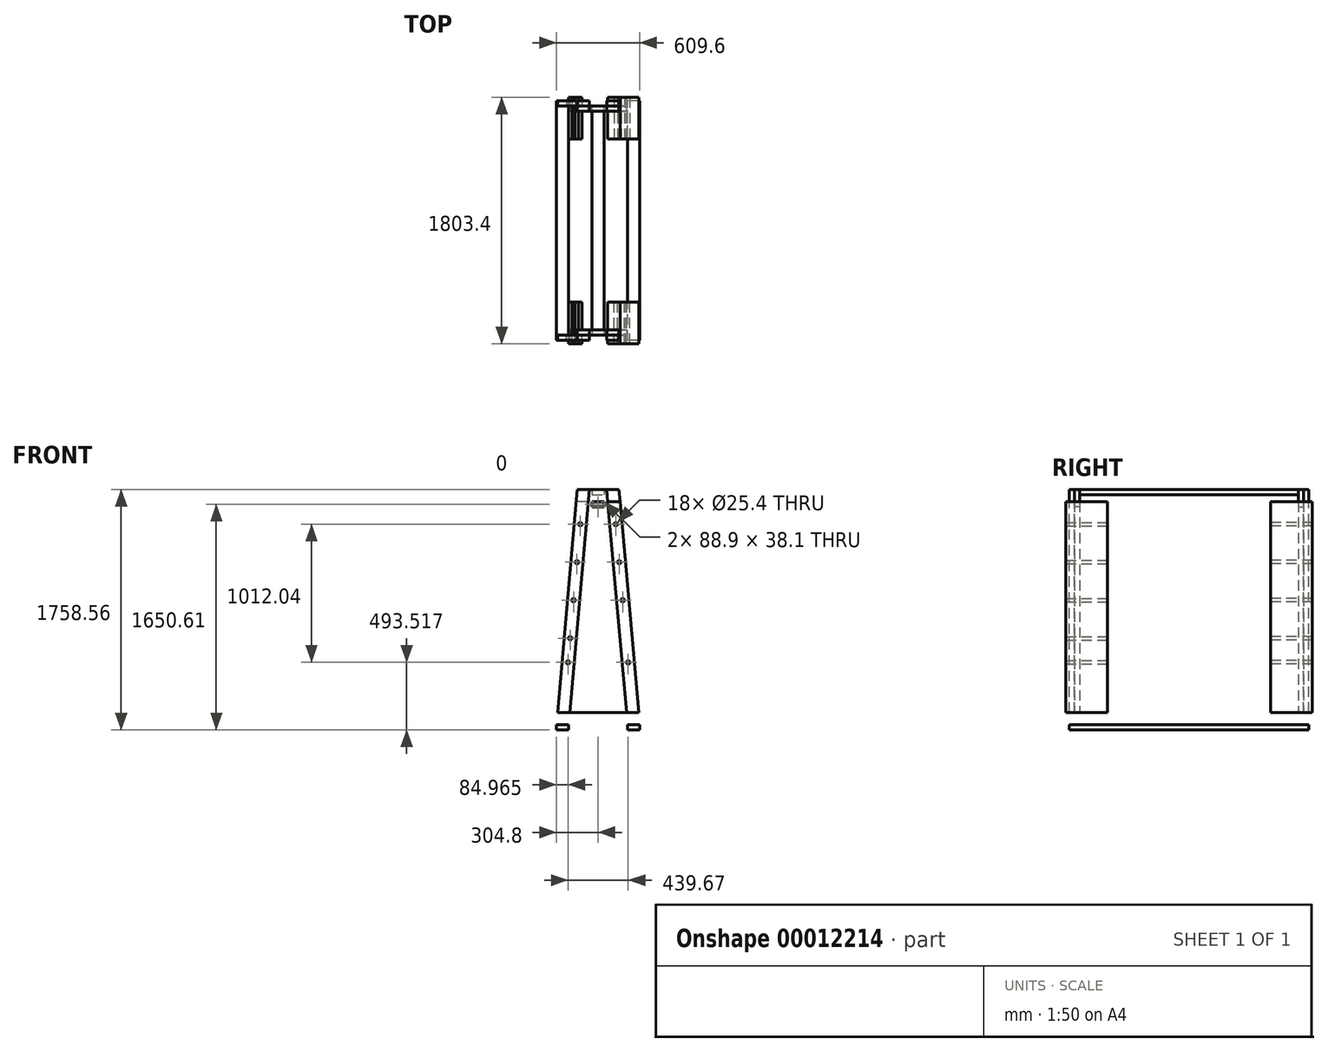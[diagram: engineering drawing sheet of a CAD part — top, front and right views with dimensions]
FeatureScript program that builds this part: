
annotation { "Feature Type Name" : "Feature", "Feature Type Description" : "" }
export const myFeature = defineFeature(function(context is Context, id is Id, definition is map)
    precondition{}
    {
        {
            var Q0;
            Q0=qCreatedBy(makeId("Front.planeOp"),FACE);
            var sketch = newSketch(context, id + "F0", { "sketchPlane" : qUnion([Q0])});
            skLineSegment(sketch, "E0", {"start": v(-304.8, 0) * mm, "end": v(-152.4, 1720.46) * mm});
            skLineSegment(sketch, "E1", {"start": v(-152.4, 1720.46) * mm, "end": v(-63.15, 1720.46) * mm});
            skLineSegment(sketch, "E2", {"start": v(-63.15, 1720.46) * mm, "end": v(-215.55, 0) * mm});
            skLineSegment(sketch, "E3", {"start": v(-215.55, 0) * mm, "end": v(-304.8, 0) * mm});
            skLineSegment(sketch, "E4", {"start": v(215.55, 0) * mm, "end": v(63.15, 1720.46) * mm});
            skLineSegment(sketch, "E5", {"start": v(63.15, 1720.46) * mm, "end": v(152.4, 1720.46) * mm});
            skLineSegment(sketch, "E6", {"start": v(152.4, 1720.46) * mm, "end": v(304.8, 0) * mm});
            skLineSegment(sketch, "E7", {"start": v(304.8, 0) * mm, "end": v(215.55, 0) * mm});
            skLineSegment(sketch, "E8", {"start": v(-107.78, 1720.46) * mm, "end": v(-260.18, 0) * mm, "construction": true});
            skCircle(sketch, "E9", {"center": v(-219.83, 455.42) * mm, "radius": 12.7 * mm});
            skCircle(sketch, "E10", {"center": v(-179.5, 910.83) * mm, "radius": 12.7 * mm});
            skCircle(sketch, "E11", {"center": v(-154.84, 1189.14) * mm, "radius": 12.7 * mm});
            skCircle(sketch, "E12", {"center": v(-130.19, 1467.45) * mm, "radius": 12.7 * mm});
            skLineSegment(sketch, "E13", {"start": v(-63.15, 1720.46) * mm, "end": v(63.15, 1720.46) * mm});
            skLineSegment(sketch, "E14", {"start": v(160.27, 1631.56) * mm, "end": v(-160.27, 1631.56) * mm});
            skLineSegment(sketch, "E15", {"start": v(-215.55, 0) * mm, "end": v(215.55, 0) * mm});
            skLineSegment(sketch, "E16", {"start": v(-296.93, 88.9) * mm, "end": v(296.93, 88.9) * mm});
            skLineSegment(sketch, "E17.bottom", {"start": v(-304.8, 0) * mm, "end": v(304.8, 0) * mm});
            skLineSegment(sketch, "E17.left", {"start": v(-304.8, 0) * mm, "end": v(-304.8, -38.1) * mm});
            skLineSegment(sketch, "E17.right", {"start": v(304.8, 0) * mm, "end": v(304.8, -38.1) * mm});
            skLineSegment(sketch, "E18.bottom", {"start": v(-304.8, -38.1) * mm, "end": v(-215.9, -38.1) * mm});
            skLineSegment(sketch, "E19.bottom", {"start": v(304.8, -38.1) * mm, "end": v(215.9, -38.1) * mm});
            skCircle(sketch, "E20.0.MirrorC", {"center": v(130.19, 1467.45) * mm, "radius": 12.7 * mm});
            skCircle(sketch, "E21.0.MirrorC", {"center": v(154.84, 1189.14) * mm, "radius": 12.7 * mm});
            skCircle(sketch, "E22.0.MirrorC", {"center": v(179.5, 910.83) * mm, "radius": 12.7 * mm});
            skCircle(sketch, "E23.0.MirrorC", {"center": v(219.83, 455.42) * mm, "radius": 12.7 * mm});
            skLineSegment(sketch, "E24.bottom", {"start": v(-44.45, 1720.46) * mm, "end": v(44.45, 1720.46) * mm});
            skLineSegment(sketch, "E24.top", {"start": v(-44.45, 1758.56) * mm, "end": v(44.45, 1758.56) * mm});
            skLineSegment(sketch, "E24.left", {"start": v(-44.45, 1720.46) * mm, "end": v(-44.45, 1758.56) * mm});
            skLineSegment(sketch, "E24.right", {"start": v(44.45, 1720.46) * mm, "end": v(44.45, 1758.56) * mm});
            skLineSegment(sketch, "E25.bottom", {"start": v(44.45, 1631.56) * mm, "end": v(-44.45, 1631.56) * mm});
            skLineSegment(sketch, "E25.top", {"start": v(44.45, 1593.46) * mm, "end": v(-44.45, 1593.46) * mm});
            skLineSegment(sketch, "E25.left", {"start": v(44.45, 1631.56) * mm, "end": v(44.45, 1593.46) * mm});
            skLineSegment(sketch, "E25.right", {"start": v(-44.45, 1631.56) * mm, "end": v(-44.45, 1593.46) * mm});
            skLineSegment(sketch, "E26", {"start": v(215.9, -38.1) * mm, "end": v(215.55, 0) * mm});
            skLineSegment(sketch, "E27", {"start": v(-215.9, -38.1) * mm, "end": v(-215.55, 0) * mm});
            skCircle(sketch, "E28", {"center": v(-204.15, 632.52) * mm, "radius": 12.7 * mm});
            skSolve(sketch);
        }
        {
            var Q0;
            {var subQ5=sQuery(id+"F0.wireOp",EDGE,"E1");Q0=makeQuery(id+"F0.imprint","IMPRINT",FACE,{"disambiguationData":[TD([[makeQuery(id+"F0.imprint","IMPRINT",EDGE,{"derivedFrom":subQ5}),-1.0]])]});}
            var Q1;
            {var subQ5=sQuery(id+"F0.wireOp",EDGE,"E5");Q1=makeQuery(id+"F0.imprint","IMPRINT",FACE,{"disambiguationData":[TD([[makeQuery(id+"F0.imprint","IMPRINT",EDGE,{"derivedFrom":subQ5}),-1.0]])]});}
            var Q2;
            {var subQ0=sQuery(id+"F0.wireOp",EDGE,"E17.bottom");var subQ1=sQuery(id+"F0.wireOp",EDGE,"E2");var subQ2=makeQuery(id+"F0.imprint","INTERSECT",VERTEX,{"derivedFrom":[subQ1,subQ0]});Q2=makeQuery(id+"F0.imprint","IMPRINT",FACE,{"disambiguationData":[TD([[makeQuery(id+"F0.imprint","IMPRINT",EDGE,{"disambiguationData":[TD([[subQ2,1.0]])],"derivedFrom":subQ1}),-1.0]])]});}
            var Q3;
            {var subQ0=sQuery(id+"F0.wireOp",EDGE,"E17.bottom");var subQ3=sQuery(id+"F0.wireOp",EDGE,"E4");var subQ4=makeQuery(id+"F0.imprint","INTERSECT",VERTEX,{"derivedFrom":[subQ3,subQ0]});Q3=makeQuery(id+"F0.imprint","IMPRINT",FACE,{"disambiguationData":[TD([[makeQuery(id+"F0.imprint","IMPRINT",EDGE,{"disambiguationData":[TD([[subQ4,-1.0]])],"derivedFrom":subQ3}),-1.0]])]});}
            var Q4;
            Q4=makeQuery(id+"F0.imprint","IMPRINT",FACE,{"disambiguationData":[TD([[makeQuery(id+"F0.imprint","IMPRINT",EDGE,{"derivedFrom":sQuery(id+"F0.wireOp",EDGE,"E9")}),-1.0]])]});
            var Q5;
            Q5=makeQuery(id+"F0.imprint","IMPRINT",FACE,{"disambiguationData":[TD([[makeQuery(id+"F0.imprint","IMPRINT",EDGE,{"derivedFrom":sQuery(id+"F0.wireOp",EDGE,"E20.0.MirrorC")}),1.0]])]});
            extrude(context, id + "F1", {"entities" : qUnion([Q0, Q1, Q2, Q3, Q4, Q5]), "depth" : 38.1 * mm});
        }
        {
            var Q0;
            {var subQ0=sQuery(id+"F0.wireOp",EDGE,"E24.bottom");Q0=makeQuery(id+"F0.imprint","IMPRINT",FACE,{"disambiguationData":[TD([[makeQuery(id+"F0.imprint","IMPRINT",EDGE,{"derivedFrom":subQ0}),-1.0]])]});}
            var Q1;
            {var subQ5=sQuery(id+"F0.wireOp",EDGE,"E5");Q1=makeQuery(id+"F0.imprint","IMPRINT",FACE,{"disambiguationData":[TD([[makeQuery(id+"F0.imprint","IMPRINT",EDGE,{"derivedFrom":subQ5}),-1.0]])]});}
            var Q2;
            {var subQ5=sQuery(id+"F0.wireOp",EDGE,"E1");Q2=makeQuery(id+"F0.imprint","IMPRINT",FACE,{"disambiguationData":[TD([[makeQuery(id+"F0.imprint","IMPRINT",EDGE,{"derivedFrom":subQ5}),-1.0]])]});}
            extrude(context, id + "F2", {"entities" : qUnion([Q0, Q1, Q2]), "oppositeDirection" : true, "depth" : 38.1 * mm});
        }
        {
            var Q0;
            {var subQ0=sQuery(id+"F0.wireOp",EDGE,"E17.bottom");var subQ3=sQuery(id+"F0.wireOp",EDGE,"E2");var subQ4=makeQuery(id+"F0.imprint","INTERSECT",VERTEX,{"derivedFrom":[subQ3,subQ0]});Q0=makeQuery(id+"F0.imprint","IMPRINT",FACE,{"disambiguationData":[TD([[makeQuery(id+"F0.imprint","IMPRINT",EDGE,{"disambiguationData":[TD([[subQ4,1.0]])],"derivedFrom":subQ3}),1.0]])]});}
            var Q1;
            {var subQ0=sQuery(id+"F0.wireOp",EDGE,"E17.bottom");var subQ1=sQuery(id+"F0.wireOp",EDGE,"E2");var subQ2=makeQuery(id+"F0.imprint","INTERSECT",VERTEX,{"derivedFrom":[subQ1,subQ0]});Q1=makeQuery(id+"F0.imprint","IMPRINT",FACE,{"disambiguationData":[TD([[makeQuery(id+"F0.imprint","IMPRINT",EDGE,{"disambiguationData":[TD([[subQ2,1.0]])],"derivedFrom":subQ1}),-1.0]])]});}
            var Q2;
            {var subQ0=sQuery(id+"F0.wireOp",EDGE,"E17.bottom");var subQ3=sQuery(id+"F0.wireOp",EDGE,"E4");var subQ4=makeQuery(id+"F0.imprint","INTERSECT",VERTEX,{"derivedFrom":[subQ3,subQ0]});Q2=makeQuery(id+"F0.imprint","IMPRINT",FACE,{"disambiguationData":[TD([[makeQuery(id+"F0.imprint","IMPRINT",EDGE,{"disambiguationData":[TD([[subQ4,-1.0]])],"derivedFrom":subQ3}),-1.0]])]});}
            extrude(context, id + "F3", {"entities" : qUnion([Q0, Q1, Q2]), "oppositeDirection" : true, "depth" : 38.1 * mm});
        }
        {
            var Q0;
            {var subQ1=sQuery(id+"F0.wireOp",EDGE,"E17.left");Q0=makeQuery(id+"F0.imprint","IMPRINT",FACE,{"disambiguationData":[TD([[makeQuery(id+"F0.imprint","IMPRINT",EDGE,{"derivedFrom":subQ1}),1.0]])]});}
            var Q1;
            {var subQ1=sQuery(id+"F0.wireOp",EDGE,"E17.right");Q1=makeQuery(id+"F0.imprint","IMPRINT",FACE,{"disambiguationData":[TD([[makeQuery(id+"F0.imprint","IMPRINT",EDGE,{"derivedFrom":subQ1}),-1.0]])]});}
            extrude(context, id + "F4", {"entities" : qUnion([Q0, Q1]), "depth" : 38.1 * mm, "hasSecondDirection" : true, "secondDirectionOppositeDirection" : true, "secondDirectionDepth" : 1714.5 * mm});
        }
        {
            var Q0;
            Q0=makeQuery(id+"F1.opExtrude","CAP_FACE",FACE,{"disambiguationData":[OSD([sQuery(id+"F0.wireOp",EDGE,"E0"),sQuery(id+"F0.wireOp",EDGE,"E1"),sQuery(id+"F0.wireOp",EDGE,"E2"),sQuery(id+"F0.wireOp",EDGE,"E9"),sQuery(id+"F0.wireOp",EDGE,"E10"),sQuery(id+"F0.wireOp",EDGE,"E11"),sQuery(id+"F0.wireOp",EDGE,"E12"),sQuery(id+"F0.wireOp",EDGE,"E17.bottom")])],"isStart":true});
            cPlane(context, id + "F5", {"entities" : qUnion([Q0]), "cplaneType" : CPlaneType.OFFSET, "offset" : 838.2 * mm, "width" : 152.4 * mm, "height" : 152.4 * mm});
        }
        {
            var Q0;
            Q0=makeQuery(id+"F0.imprint","IMPRINT",FACE,{"disambiguationData":[TD([[makeQuery(id+"F0.imprint","IMPRINT",EDGE,{"derivedFrom":sQuery(id+"F0.wireOp",EDGE,"E12")}),1.0]])]});
            var Q1;
            Q1=makeQuery(id+"F0.imprint","IMPRINT",FACE,{"disambiguationData":[TD([[makeQuery(id+"F0.imprint","IMPRINT",EDGE,{"derivedFrom":sQuery(id+"F0.wireOp",EDGE,"E11")}),1.0]])]});
            var Q2;
            Q2=makeQuery(id+"F0.imprint","IMPRINT",FACE,{"disambiguationData":[TD([[makeQuery(id+"F0.imprint","IMPRINT",EDGE,{"derivedFrom":sQuery(id+"F0.wireOp",EDGE,"E20.0.MirrorC")}),-1.0]])]});
            var Q3;
            Q3=makeQuery(id+"F0.imprint","IMPRINT",FACE,{"disambiguationData":[TD([[makeQuery(id+"F0.imprint","IMPRINT",EDGE,{"derivedFrom":sQuery(id+"F0.wireOp",EDGE,"E21.0.MirrorC")}),-1.0]])]});
            var Q4;
            Q4=makeQuery(id+"F0.imprint","IMPRINT",FACE,{"disambiguationData":[TD([[makeQuery(id+"F0.imprint","IMPRINT",EDGE,{"derivedFrom":sQuery(id+"F0.wireOp",EDGE,"E22.0.MirrorC")}),-1.0]])]});
            var Q5;
            Q5=makeQuery(id+"F0.imprint","IMPRINT",FACE,{"disambiguationData":[TD([[makeQuery(id+"F0.imprint","IMPRINT",EDGE,{"derivedFrom":sQuery(id+"F0.wireOp",EDGE,"E10")}),1.0]])]});
            var Q6;
            Q6=makeQuery(id+"F0.imprint","IMPRINT",FACE,{"disambiguationData":[TD([[makeQuery(id+"F0.imprint","IMPRINT",EDGE,{"derivedFrom":sQuery(id+"F0.wireOp",EDGE,"E23.0.MirrorC")}),-1.0]])]});
            var Q7;
            Q7=makeQuery(id+"F0.imprint","IMPRINT",FACE,{"disambiguationData":[TD([[makeQuery(id+"F0.imprint","IMPRINT",EDGE,{"derivedFrom":sQuery(id+"F0.wireOp",EDGE,"E28")}),1.0]])]});
            extrude(context, id + "F6", {"entities" : qUnion([Q0, Q1, Q2, Q3, Q4, Q5, Q6, Q7]), "depth" : 63.5 * mm, "hasSecondDirection" : true, "secondDirectionOppositeDirection" : true, "secondDirectionDepth" : 241.3 * mm});
        }
        {
            var Q0;
            Q0=makeQuery(id+"F1.opExtrude","SWEPT_BODY",BODY,{"disambiguationData":[OSD([sQuery(id+"F0.wireOp",EDGE,"E0"),sQuery(id+"F0.wireOp",EDGE,"E1"),sQuery(id+"F0.wireOp",EDGE,"E2"),sQuery(id+"F0.wireOp",EDGE,"E9"),sQuery(id+"F0.wireOp",EDGE,"E10"),sQuery(id+"F0.wireOp",EDGE,"E11"),sQuery(id+"F0.wireOp",EDGE,"E12"),sQuery(id+"F0.wireOp",EDGE,"E17.bottom")])]});
            var Q1;
            Q1=makeQuery(id+"F2.opExtrude","SWEPT_BODY",BODY,{"disambiguationData":[OSD([sQuery(id+"F0.wireOp",EDGE,"E0"),sQuery(id+"F0.wireOp",EDGE,"E1"),sQuery(id+"F0.wireOp",EDGE,"E5"),sQuery(id+"F0.wireOp",EDGE,"E6"),sQuery(id+"F0.wireOp",EDGE,"E13"),sQuery(id+"F0.wireOp",EDGE,"E14"),sQuery(id+"F0.wireOp",EDGE,"E24.bottom"),sQuery(id+"F0.wireOp",EDGE,"E25.bottom")])]});
            var Q2;
            Q2=makeQuery(id+"F3.opExtrude","SWEPT_BODY",BODY,{"disambiguationData":[OSD([sQuery(id+"F0.wireOp",EDGE,"E0"),sQuery(id+"F0.wireOp",EDGE,"E6"),sQuery(id+"F0.wireOp",EDGE,"E16"),sQuery(id+"F0.wireOp",EDGE,"E17.bottom")])]});
            var Q3;
            Q3=makeQuery(id+"F1.opExtrude","SWEPT_BODY",BODY,{"disambiguationData":[OSD([sQuery(id+"F0.wireOp",EDGE,"E4"),sQuery(id+"F0.wireOp",EDGE,"E5"),sQuery(id+"F0.wireOp",EDGE,"E6"),sQuery(id+"F0.wireOp",EDGE,"E17.bottom"),sQuery(id+"F0.wireOp",EDGE,"E20.0.MirrorC"),sQuery(id+"F0.wireOp",EDGE,"E21.0.MirrorC"),sQuery(id+"F0.wireOp",EDGE,"E22.0.MirrorC"),sQuery(id+"F0.wireOp",EDGE,"E23.0.MirrorC")])]});
            var Q4;
            Q4=makeQuery(id+"F6.opExtrude","SWEPT_BODY",BODY,{"disambiguationData":[OSD([sQuery(id+"F0.wireOp",EDGE,"E22.0.MirrorC")])]});
            var Q5;
            Q5=makeQuery(id+"F6.opExtrude","SWEPT_BODY",BODY,{"disambiguationData":[OSD([sQuery(id+"F0.wireOp",EDGE,"E23.0.MirrorC")])]});
            var Q6;
            Q6=makeQuery(id+"F6.opExtrude","SWEPT_BODY",BODY,{"disambiguationData":[OSD([sQuery(id+"F0.wireOp",EDGE,"E20.0.MirrorC")])]});
            var Q7;
            Q7=makeQuery(id+"F6.opExtrude","SWEPT_BODY",BODY,{"disambiguationData":[OSD([sQuery(id+"F0.wireOp",EDGE,"E12")])]});
            var Q8;
            Q8=makeQuery(id+"F6.opExtrude","SWEPT_BODY",BODY,{"disambiguationData":[OSD([sQuery(id+"F0.wireOp",EDGE,"E21.0.MirrorC")])]});
            var Q9;
            Q9=makeQuery(id+"F6.opExtrude","SWEPT_BODY",BODY,{"disambiguationData":[OSD([sQuery(id+"F0.wireOp",EDGE,"E11")])]});
            var Q10;
            Q10=makeQuery(id+"F6.opExtrude","SWEPT_BODY",BODY,{"disambiguationData":[OSD([sQuery(id+"F0.wireOp",EDGE,"E9")])]});
            var Q11;
            Q11=makeQuery(id+"F6.opExtrude","SWEPT_BODY",BODY,{"disambiguationData":[OSD([sQuery(id+"F0.wireOp",EDGE,"E10")])]});
            var Q12;
            Q12=makeQuery(id+"F6.opExtrude","SWEPT_BODY",BODY,{"disambiguationData":[OSD([sQuery(id+"F0.wireOp",EDGE,"E28")])]});
            var Q13;
            Q13=qCreatedBy(id+"F5.planeOp",FACE);
            mirror(context, id + "F7", {"entities" : qUnion([Q0, Q1, Q2, Q3, Q4, Q5, Q6, Q7, Q8, Q9, Q10, Q11, Q12]), "mirrorPlane" : qUnion([Q13])});
        }
        {
            var Q0;
            Q0=makeQuery(id+"F7.opPattern","COPY",FACE,{"derivedFrom":makeQuery(id+"F2.opExtrude","CAP_FACE",FACE,{"disambiguationData":[OSD([sQuery(id+"F0.wireOp",EDGE,"E0"),sQuery(id+"F0.wireOp",EDGE,"E1"),sQuery(id+"F0.wireOp",EDGE,"E5"),sQuery(id+"F0.wireOp",EDGE,"E6"),sQuery(id+"F0.wireOp",EDGE,"E13"),sQuery(id+"F0.wireOp",EDGE,"E14"),sQuery(id+"F0.wireOp",EDGE,"E24.bottom"),sQuery(id+"F0.wireOp",EDGE,"E25.bottom")])],"isStart":false}),"instanceName":"1"});
            var sketch = newSketch(context, id + "F8", { "sketchPlane" : qUnion([Q0])});
            skLineSegment(sketch, "E29.bottom", {"start": v(-44.45, 1720.46) * mm, "end": v(44.45, 1720.46) * mm});
            skLineSegment(sketch, "E29.top", {"start": v(-44.45, 1682.36) * mm, "end": v(44.45, 1682.36) * mm});
            skLineSegment(sketch, "E29.left", {"start": v(-44.45, 1720.46) * mm, "end": v(-44.45, 1682.36) * mm});
            skLineSegment(sketch, "E29.right", {"start": v(44.45, 1720.46) * mm, "end": v(44.45, 1682.36) * mm});
            skSolve(sketch);
        }
        {
            var Q0;
            Q0=makeQuery(id+"F8.imprint","IMPRINT",FACE,{"disambiguationData":[TD([[makeQuery(id+"F8.imprint","IMPRINT",EDGE,{"derivedFrom":sQuery(id+"F8.wireOp",EDGE,"E29.bottom")}),-1.0]])]});
            var Q1;
            Q1=makeQuery(id+"F2.opExtrude","SWEPT_BODY",BODY,{"disambiguationData":[OSD([sQuery(id+"F0.wireOp",EDGE,"E0"),sQuery(id+"F0.wireOp",EDGE,"E1"),sQuery(id+"F0.wireOp",EDGE,"E5"),sQuery(id+"F0.wireOp",EDGE,"E6"),sQuery(id+"F0.wireOp",EDGE,"E13"),sQuery(id+"F0.wireOp",EDGE,"E14"),sQuery(id+"F0.wireOp",EDGE,"E24.bottom"),sQuery(id+"F0.wireOp",EDGE,"E25.bottom")])]});
            extrude(context, id + "F9", {"entities" : qUnion([Q0]), "endBound" : BoundingType.UP_TO_NEXT, "endBoundEntity" : qUnion([Q1]), "depth" : 25.4 * mm});
        }
    });
